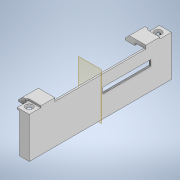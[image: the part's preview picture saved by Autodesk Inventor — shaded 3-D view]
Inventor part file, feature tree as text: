
AUTODESK INVENTOR PART (.ipt)
format: ipt  version: 2020.1 (Build 241239000, 239)  size: 236,544 bytes
history: native  units: mm
features: sketch x9, extrude x7, chamfer x3, projected_geometry x3, hole x2, mirror x2, plane x1
ambient origin geometry x8: Origin, YZ Plane, XZ Plane, XY Plane, X Axis, Y Axis, Z Axis, Center Point
bodies: Solid1 (feature_tree)
feature tree (27):
  extrude  "Extrusion1"  Depth=47.4mm
  extrude  "Extrusion2"  Depth=2.0mm
  extrude  "Extrusion3"  Depth=2.0mm
  extrude  "Extrusion4"  Depth=12.0mm
  chamfer  "Chamfer1"  Distance=4.0mm
  chamfer  "Chamfer2"  Distance=3.0mm
  extrude  "Extrusion5"  Depth=5.0mm TaperAngle=45.0deg
  plane  "Work Plane1"
  hole  "Hole1"  [1 undecoded]
  extrude  "Extrusion6"  Depth=2.0mm
  chamfer  "Chamfer3"  Distance=8.0mm
  mirror  "Mirror2"
  hole  "Hole2"  [1 undecoded]
  mirror  "Mirror3"
  extrude  "Extrusion7"  Depth=14.5mm
  sketch  "Sketch1"  dims[d0=172.0mm d1=47.4mm]
  sketch  "Sketch2"  dims[d2=2.0mm d3=0.0mm d4=2.0mm]
  sketch  "Sketch3"  dims[d5=2.0mm d6=2.0mm]
  sketch  "Sketch4"  dims[d7=10.0mm d8=0.0mm d9=12.0mm]
  projected_geometry  "Projected Loop1"
  sketch  "Sketch5"  dims[d10=25.0mm]
  sketch  "Sketch6"  dims[d11=19.0mm d12=4.0mm d13=0.0mm]
  sketch  "Sketch7"  dims[d14=12.388mm d15=3.0mm d16=0.0mm]
  sketch  "Sketch8"  dims[d17=1.0mm d18=2.0mm d19=45.0deg d20=5.0mm d21=2.0mm d22=45.0deg]
  projected_geometry  "Projected Loop2"
  projected_geometry  "Projected Loop3"
  sketch  "Sketch9"  dims[d24=10.0mm d25=0.0mm d26=14.5mm d27=2.0mm d28=8.0mm d29=8.0mm d30=4.0mm d31=6.0mm d32=8.4mm d33=2.0mm d34=90.0deg d35=10.0mm d36=20.594885mm d37=14.5mm d38=2.0mm d39=10.0mm d40=0.0mm d41=2.0mm d42=2.0mm d43=45.0deg d44=4.0mm d45=6.0mm d46=8.4mm d47=2.0mm d48=90.0deg d49=10.0mm d50=20.594885mm d51=6.0mm d52=16.0mm d53=25.0mm d54=14.0mm d55=58.0mm d56=7.0mm d57=10.0mm d58=0.0mm]
note: 2 required parameter values undecoded (feature->parameter linkage not recoverable at this tier; creation-order binding heuristic only, values carry confidence <= 0.55)
